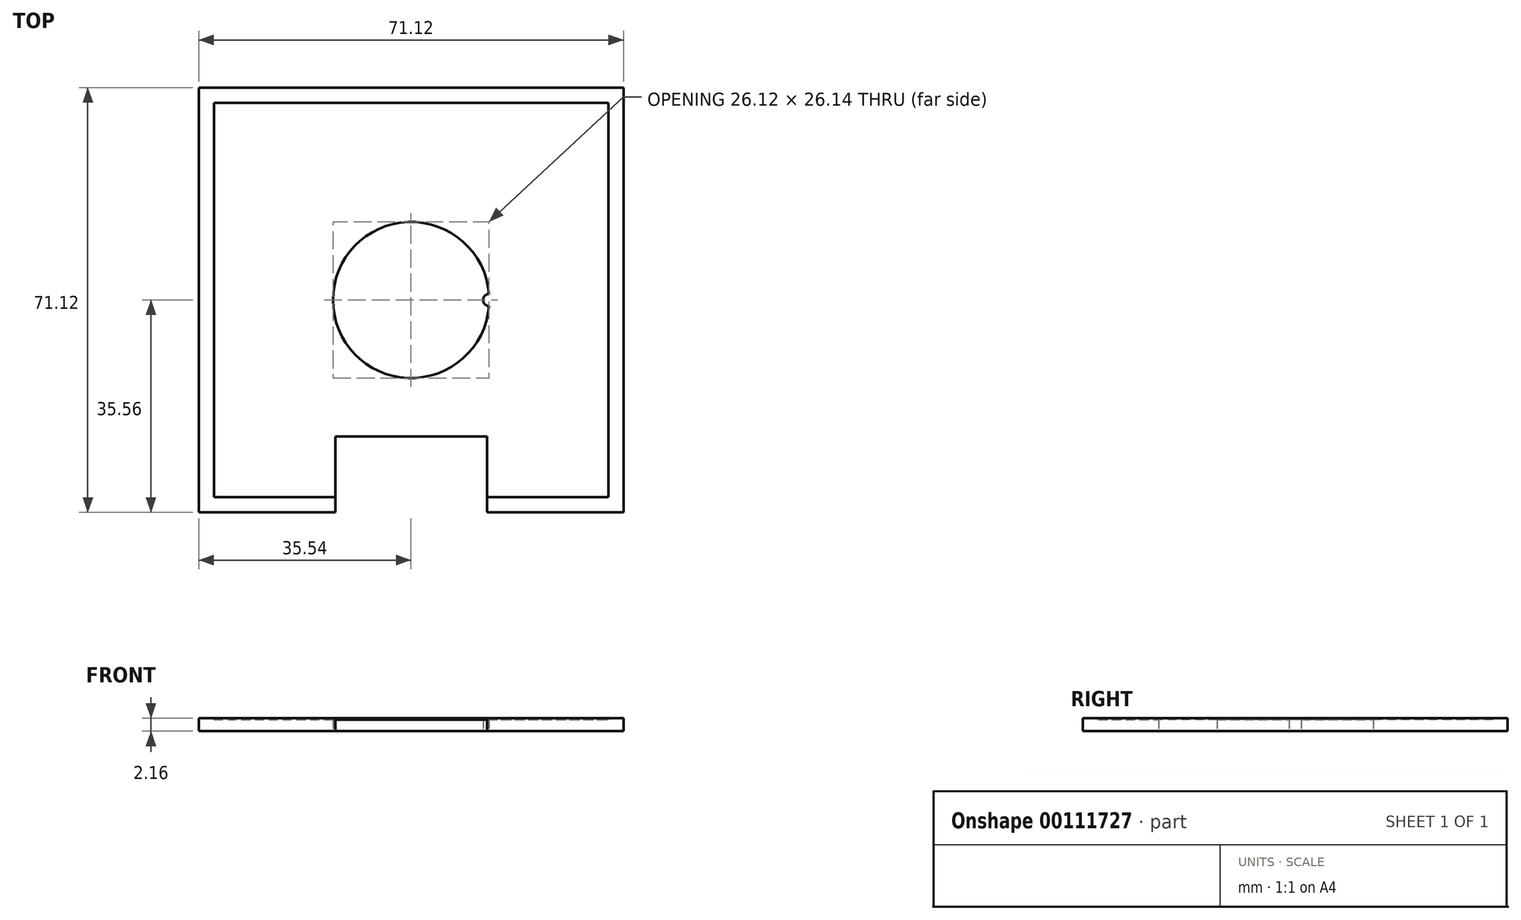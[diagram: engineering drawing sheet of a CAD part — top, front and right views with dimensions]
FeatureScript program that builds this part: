
annotation { "Feature Type Name" : "Feature", "Feature Type Description" : "" }
export const myFeature = defineFeature(function(context is Context, id is Id, definition is map)
    precondition{}
    {
        {
            var Q0;
            Q0=qCreatedBy(makeId("Top.planeOp"),FACE);
            var sketch = newSketch(context, id + "F0", { "sketchPlane" : qUnion([Q0])});
            skArc(sketch, "E0", {"start": v(13.04, 1.02) * mm, "mid": v(-13.08, 0) * mm, "end": v(13.04, -1.02) * mm});
            skArc(sketch, "E1", {"start": v(13.04, 1.02) * mm, "mid": v(12.07, 0) * mm, "end": v(13.04, -1.02) * mm});
            skLineSegment(sketch, "E2.bottom", {"start": v(-33.02, 33.02) * mm, "end": v(33.02, 33.02) * mm});
            skLineSegment(sketch, "E2.top", {"start": v(-33.02, -33.02) * mm, "end": v(33.02, -33.02) * mm});
            skLineSegment(sketch, "E2.left", {"start": v(-33.02, 33.02) * mm, "end": v(-33.02, -33.02) * mm});
            skLineSegment(sketch, "E2.right", {"start": v(33.02, 33.02) * mm, "end": v(33.02, -33.02) * mm});
            skLineSegment(sketch, "E3.bottom", {"start": v(35.56, 35.56) * mm, "end": v(-35.56, 35.56) * mm});
            skLineSegment(sketch, "E3.top", {"start": v(35.56, -35.56) * mm, "end": v(-35.56, -35.56) * mm});
            skLineSegment(sketch, "E3.left", {"start": v(35.56, 35.56) * mm, "end": v(35.56, -35.56) * mm});
            skLineSegment(sketch, "E3.right", {"start": v(-35.56, 35.56) * mm, "end": v(-35.56, -35.56) * mm});
            skSolve(sketch);
        }
        {
            var Q0;
            Q0=makeQuery(id+"F0.imprint","IMPRINT",FACE,{"disambiguationData":[TD([[makeQuery(id+"F0.imprint","IMPRINT",EDGE,{"derivedFrom":sQuery(id+"F0.wireOp",EDGE,"E0")}),-1.0]])]});
            extrude(context, id + "F1", {"entities" : qUnion([Q0]), "depth" : 1.9 * mm});
        }
        {
            var Q0;
            Q0 = qSketchRegion(id + "F0", true);
            extrude(context, id + "F2", {"entities" : qUnion([Q0]), "operationType" : NewBodyOperationType.ADD, "depth" : 2.16 * mm});
        }
        {
            var Q0;
            {var subQ0=sQuery(id+"F0.wireOp",EDGE,"E2.right");var subQ1=sQuery(id+"F0.wireOp",EDGE,"E2.left");var subQ2=sQuery(id+"F0.wireOp",EDGE,"E2.top");var subQ3=sQuery(id+"F0.wireOp",EDGE,"E2.bottom");Q0=makeQuery(id+"F2.boolean.opBoolean","MERGE",FACE,{"derivedFrom":[makeQuery(id+"F1.opExtrude","CAP_FACE",FACE,{"disambiguationData":[OSD([sQuery(id+"F0.wireOp",EDGE,"E0"),sQuery(id+"F0.wireOp",EDGE,"E1"),subQ3,subQ2,subQ1,subQ0])],"isStart":true}),makeQuery(id+"F2.opExtrude","CAP_FACE",FACE,{"disambiguationData":[OSD([subQ3,subQ2,subQ1,subQ0,sQuery(id+"F0.wireOp",EDGE,"E3.bottom"),sQuery(id+"F0.wireOp",EDGE,"E3.top"),sQuery(id+"F0.wireOp",EDGE,"E3.left"),sQuery(id+"F0.wireOp",EDGE,"E3.right")])],"isStart":true})]});}
            var sketch = newSketch(context, id + "F3", { "sketchPlane" : qUnion([Q0])});
            skLineSegment(sketch, "E4.bottom", {"start": v(12.7, 22.86) * mm, "end": v(-12.7, 22.86) * mm});
            skLineSegment(sketch, "E4.top", {"start": v(12.7, 48.26) * mm, "end": v(-12.7, 48.26) * mm});
            skLineSegment(sketch, "E4.left", {"start": v(12.7, 22.86) * mm, "end": v(12.7, 48.26) * mm});
            skLineSegment(sketch, "E4.right", {"start": v(-12.7, 22.86) * mm, "end": v(-12.7, 48.26) * mm});
            skPoint(sketch, "E4.middle", {"position": v(0, 35.56) * mm});
            skSolve(sketch);
        }
        {
            var Q0;
            Q0 = qSketchRegion(id + "F3", true);
            extrude(context, id + "F4", {"entities" : qUnion([Q0]), "operationType" : NewBodyOperationType.REMOVE, "oppositeDirection" : true, "depth" : 25.4 * mm});
        }
    });
